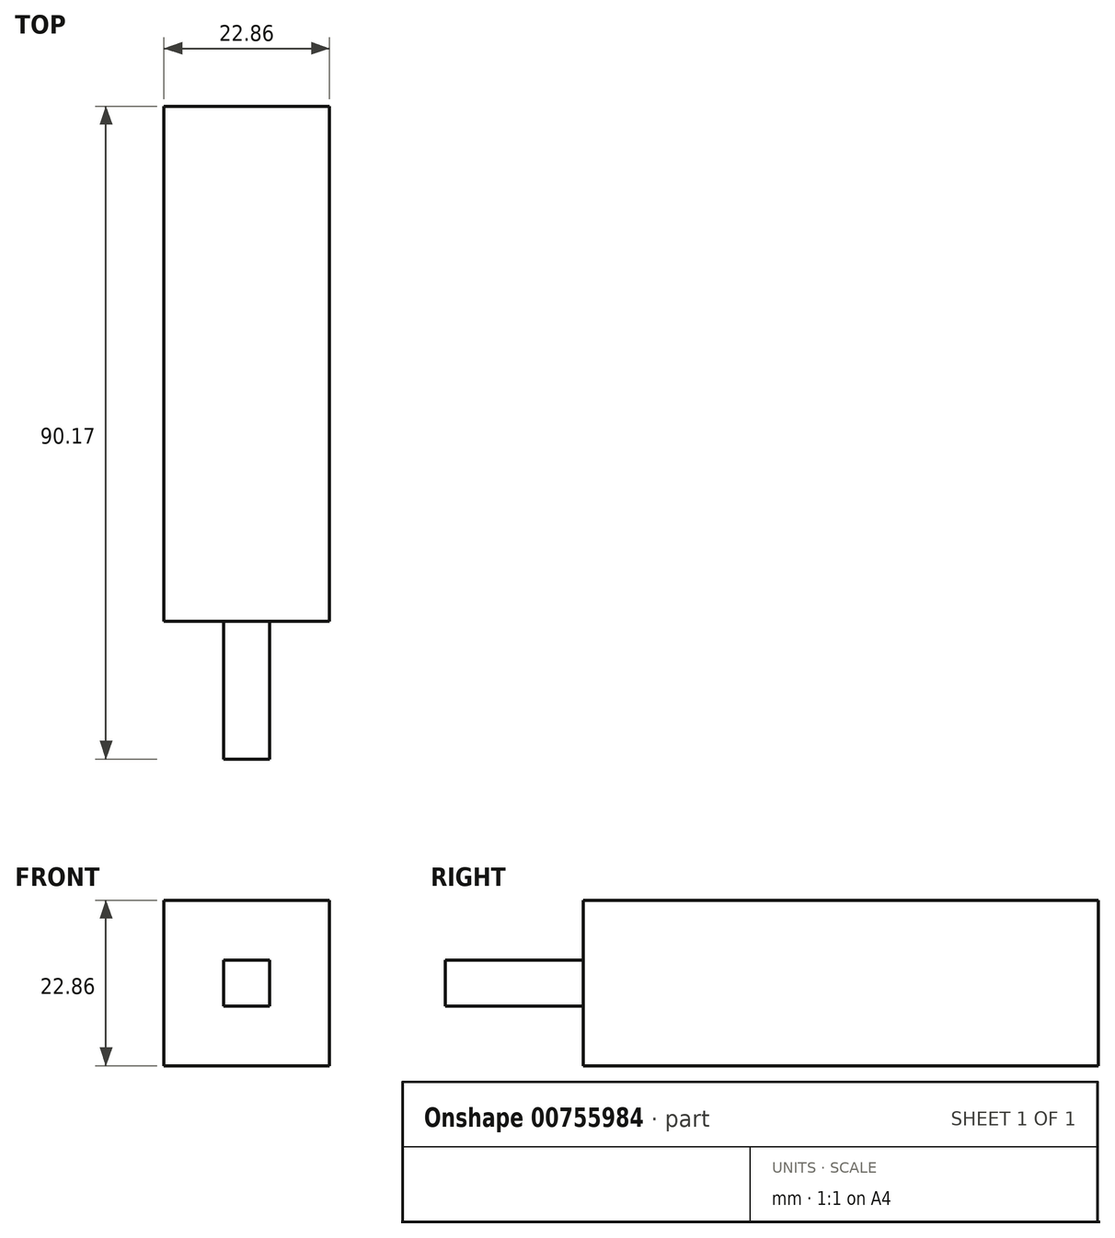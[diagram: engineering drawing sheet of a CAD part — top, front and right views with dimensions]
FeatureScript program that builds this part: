
annotation { "Feature Type Name" : "Feature", "Feature Type Description" : "" }
export const myFeature = defineFeature(function(context is Context, id is Id, definition is map)
    precondition{}
    {
        {
            var Q0;
            Q0=qCreatedBy(makeId("Top.planeOp"),FACE);
            var sketch = newSketch(context, id + "F0", { "sketchPlane" : qUnion([Q0])});
            skLineSegment(sketch, "E0.bottom", {"start": v(0, 0) * mm, "end": v(22.86, 0) * mm});
            skLineSegment(sketch, "E0.top", {"start": v(0, 71.12) * mm, "end": v(22.86, 71.12) * mm});
            skLineSegment(sketch, "E0.left", {"start": v(0, 0) * mm, "end": v(0, 71.12) * mm});
            skLineSegment(sketch, "E0.right", {"start": v(22.86, 0) * mm, "end": v(22.86, 71.12) * mm});
            skSolve(sketch);
        }
        {
            var Q0;
            Q0=qSketchRegion(id+"F0",true);
            extrude(context, id + "F1", {"entities" : qUnion([Q0]), "depth" : 22.86 * mm, "offsetDistance" : 25.4 * mm});
        }
        {
            var Q0;
            Q0=makeQuery(id+"F1.opExtrude","SWEPT_FACE",FACE,{"disambiguationData":[OSD([sQuery(id+"F0.wireOp",EDGE,"E0.bottom")])]});
            var sketch = newSketch(context, id + "F2", { "sketchPlane" : qUnion([Q0])});
            skLineSegment(sketch, "E1.bottom", {"start": v(8.26, 14.6) * mm, "end": v(14.6, 14.6) * mm});
            skLineSegment(sketch, "E1.top", {"start": v(8.26, 8.26) * mm, "end": v(14.6, 8.26) * mm});
            skLineSegment(sketch, "E1.left", {"start": v(8.26, 14.6) * mm, "end": v(8.26, 8.26) * mm});
            skLineSegment(sketch, "E1.right", {"start": v(14.6, 14.6) * mm, "end": v(14.6, 8.26) * mm});
            skPoint(sketch, "E1.middle", {"position": v(11.43, 11.43) * mm});
            skSolve(sketch);
        }
        {
            var Q0;
            Q0=qSketchRegion(id+"F2",true);
            extrude(context, id + "F3", {"entities" : qUnion([Q0]), "operationType" : NewBodyOperationType.ADD, "depth" : 19.05 * mm, "offsetDistance" : 25.4 * mm});
        }
    });
